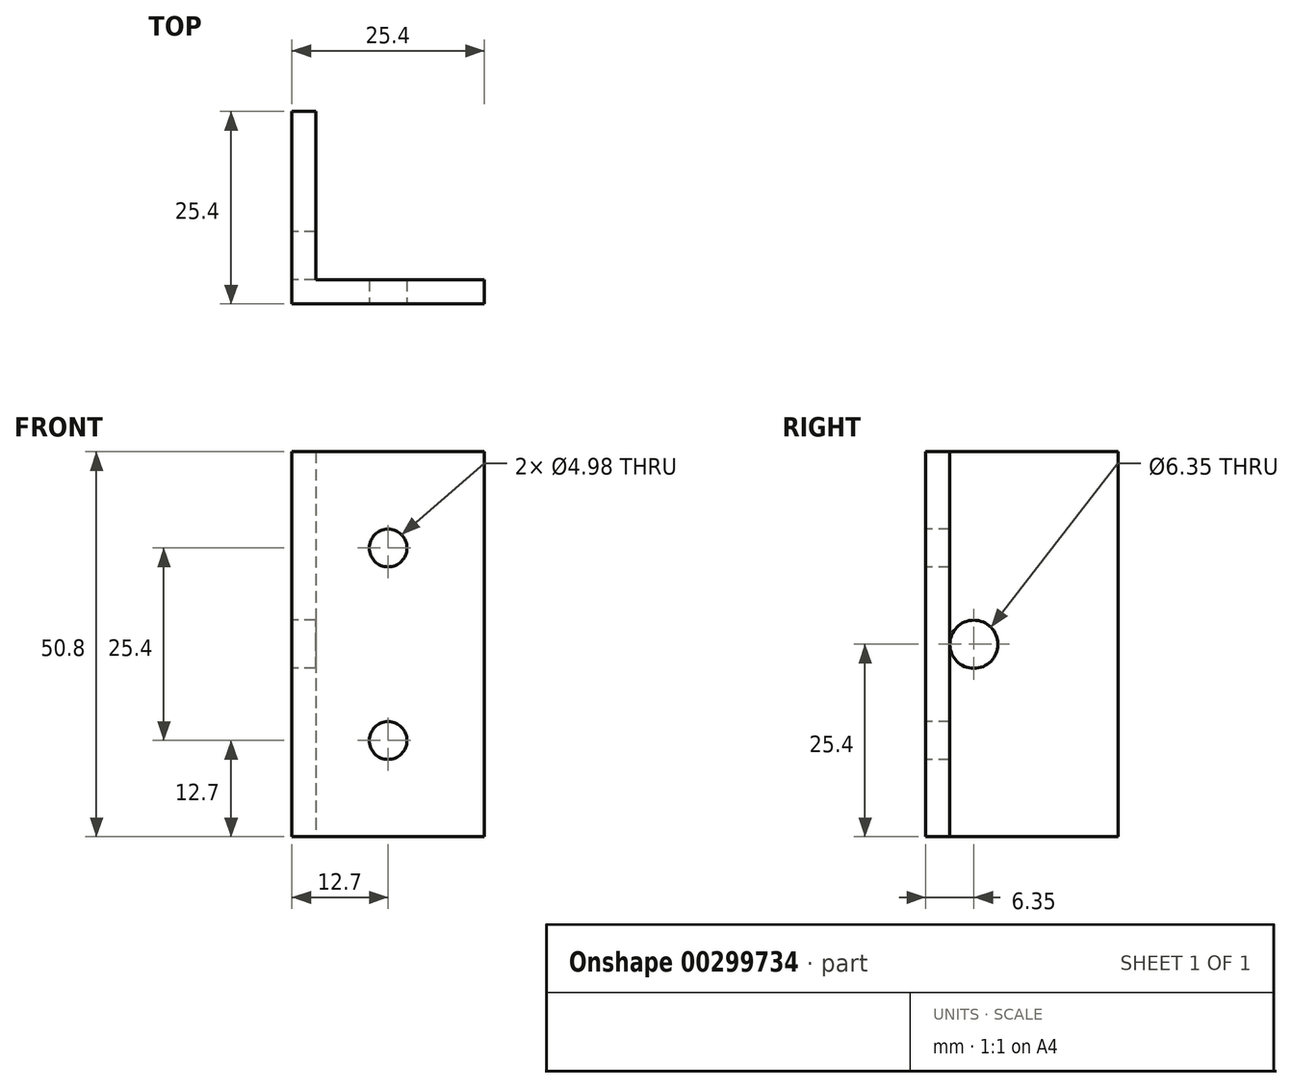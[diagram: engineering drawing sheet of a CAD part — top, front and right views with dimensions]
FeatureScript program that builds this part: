
annotation { "Feature Type Name" : "Feature", "Feature Type Description" : "" }
export const myFeature = defineFeature(function(context is Context, id is Id, definition is map)
    precondition{}
    {
        {
            var Q0;
            Q0=qCreatedBy(makeId("Top.planeOp"),FACE);
            var sketch = newSketch(context, id + "F0", { "sketchPlane" : qUnion([Q0])});
            skLineSegment(sketch, "E0", {"start": v(0, 25.4) * mm, "end": v(0, 0) * mm});
            skLineSegment(sketch, "E1", {"start": v(0, 0) * mm, "end": v(25.4, 0) * mm});
            skLineSegment(sketch, "E2", {"start": v(25.4, 0) * mm, "end": v(25.4, 3.18) * mm});
            skLineSegment(sketch, "E3", {"start": v(25.4, 3.18) * mm, "end": v(3.17, 3.17) * mm});
            skLineSegment(sketch, "E4", {"start": v(3.17, 3.17) * mm, "end": v(3.17, 25.4) * mm});
            skLineSegment(sketch, "E5", {"start": v(3.17, 25.4) * mm, "end": v(0, 25.4) * mm});
            skSolve(sketch);
        }
        {
            var Q0;
            Q0 = qSketchRegion(id + "F0", true);
            extrude(context, id + "F1", {"entities" : qUnion([Q0]), "depth" : 50.8 * mm});
        }
        {
            var Q0;
            Q0=makeQuery(id+"F1.opExtrude","SWEPT_FACE",FACE,{"disambiguationData":[OSD([sQuery(id+"F0.wireOp",EDGE,"E1")])]});
            var sketch = newSketch(context, id + "F2", { "sketchPlane" : qUnion([Q0])});
            skCircle(sketch, "E6", {"center": v(12.7, 38.1) * mm, "radius": 2.49 * mm});
            skCircle(sketch, "E7", {"center": v(12.7, 12.7) * mm, "radius": 2.49 * mm});
            skSolve(sketch);
        }
        {
            var Q0;
            Q0 = qSketchRegion(id + "F2", true);
            extrude(context, id + "F3", {"entities" : qUnion([Q0]), "operationType" : NewBodyOperationType.REMOVE, "endBound" : BoundingType.THROUGH_ALL, "oppositeDirection" : true, "depth" : 25.4 * mm});
        }
        {
            var Q0;
            Q0=makeQuery(id+"F1.opExtrude","SWEPT_FACE",FACE,{"disambiguationData":[OSD([sQuery(id+"F0.wireOp",EDGE,"E0")])]});
            var sketch = newSketch(context, id + "F4", { "sketchPlane" : qUnion([Q0])});
            skCircle(sketch, "E8", {"center": v(-6.35, 25.4) * mm, "radius": 3.18 * mm});
            skSolve(sketch);
        }
        {
            var Q0;
            Q0=makeQuery(id+"F4.imprint","IMPRINT",FACE,{"disambiguationData":[TD([[makeQuery(id+"F4.imprint","IMPRINT",EDGE,{"derivedFrom":sQuery(id+"F4.wireOp",EDGE,"E8")}),1.0]])]});
            extrude(context, id + "F5", {"entities" : qUnion([Q0]), "operationType" : NewBodyOperationType.REMOVE, "endBound" : BoundingType.THROUGH_ALL, "oppositeDirection" : true, "depth" : 25.4 * mm});
        }
    });
